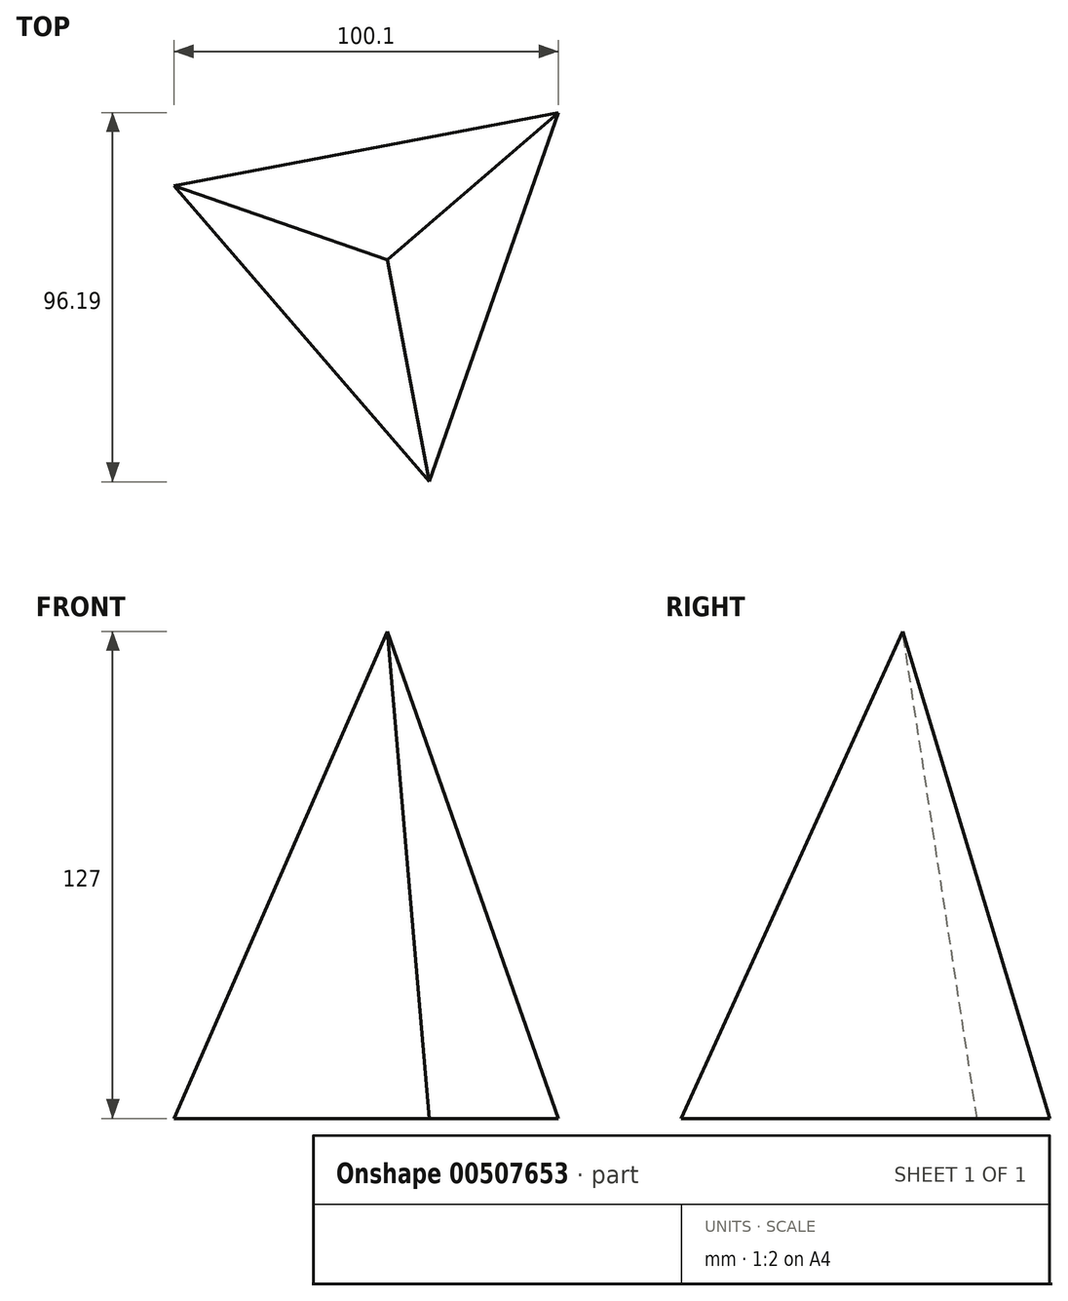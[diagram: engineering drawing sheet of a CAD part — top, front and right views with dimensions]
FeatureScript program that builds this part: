
annotation { "Feature Type Name" : "Feature", "Feature Type Description" : "" }
export const myFeature = defineFeature(function(context is Context, id is Id, definition is map)
    precondition{}
    {
        {
            var Q0;
            Q0=qCreatedBy(makeId("Top.planeOp"),FACE);
            var sketch = newSketch(context, id + "F0", { "sketchPlane" : qUnion([Q0])});
            skCircle(sketch, "E0.cCircle", {"center": v(0, 0) * mm, "radius": 58.83 * mm, "construction": true});
            skLineSegment(sketch, "E0.0", {"start": v(44.57, 38.4) * mm, "end": v(10.97, -57.8) * mm});
            skLineSegment(sketch, "E0.1", {"start": v(10.97, -57.8) * mm, "end": v(-55.53, 19.4) * mm});
            skLineSegment(sketch, "E0.2", {"start": v(-55.53, 19.4) * mm, "end": v(44.57, 38.4) * mm});
            skSolve(sketch);
        }
        {
            var Q0;
            Q0=qCreatedBy(makeId("Top.planeOp"),FACE);
            cPlane(context, id + "F1", {"entities" : qUnion([Q0]), "cplaneType" : CPlaneType.OFFSET, "offset" : 127 * mm, "width" : 152.4 * mm, "height" : 152.4 * mm});
        }
        {
            var Q0;
            Q0=qCreatedBy(id+"F1.planeOp",FACE);
            var sketch = newSketch(context, id + "F2", { "sketchPlane" : qUnion([Q0])});
            skPoint(sketch, "E1", {"position": v(0, 0) * mm});
            skSolve(sketch);
        }
        {
            var Q0;
            Q0=makeQuery(id+"F0.imprint","IMPRINT",FACE,{"disambiguationData":[TD([[makeQuery(id+"F0.imprint","IMPRINT",EDGE,{"derivedFrom":sQuery(id+"F0.wireOp",EDGE,"E0.0")}),-1.0]])]});
            var Q1;
            Q1=sQuery(id+"F2.wireOp",VERTEX,"E1");
            loft(context, id + "F3", {"sheetProfilesArray" : [{ "sheetProfileEntities" : qUnion([Q0]) }, { "sheetProfileEntities" : qUnion([Q1]) }]});
        }
    });
